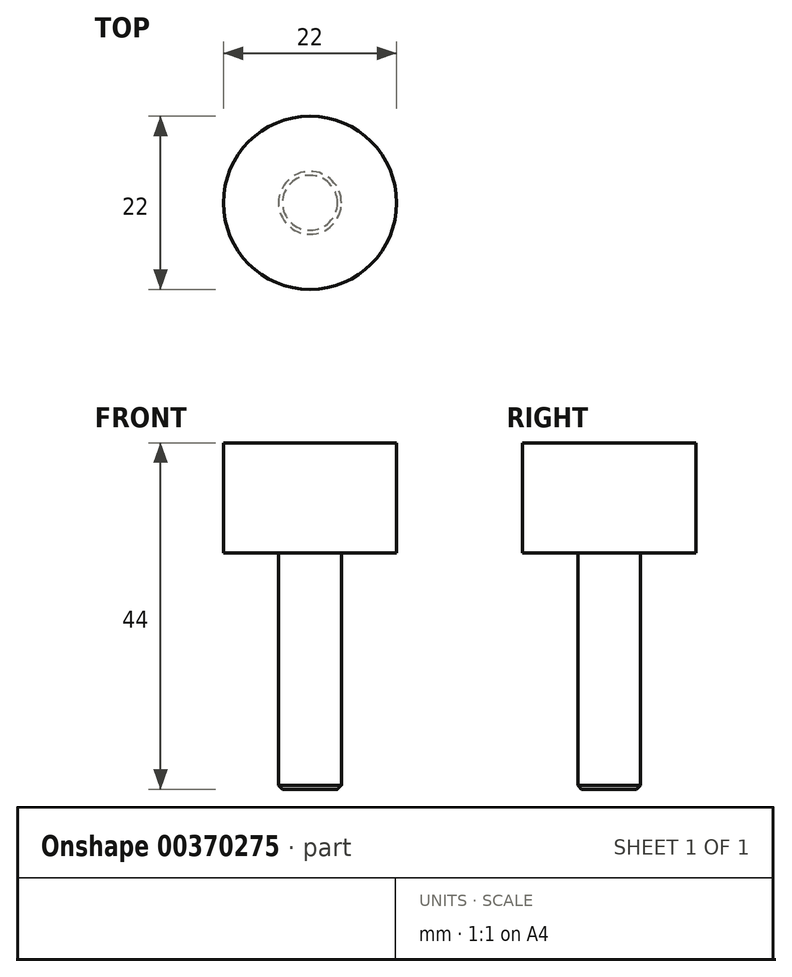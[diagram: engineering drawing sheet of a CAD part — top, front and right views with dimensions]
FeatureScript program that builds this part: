
annotation { "Feature Type Name" : "Feature", "Feature Type Description" : "" }
export const myFeature = defineFeature(function(context is Context, id is Id, definition is map)
    precondition{}
    {
        {
            var Q0;
            Q0=qCreatedBy(makeId("Top.planeOp"),FACE);
            var sketch = newSketch(context, id + "F0", { "sketchPlane" : qUnion([Q0])});
            skCircle(sketch, "E0", {"center": v(0, 0) * mm, "radius": 11 * mm});
            skSolve(sketch);
        }
        {
            var Q0;
            Q0=makeQuery(id+"F0.imprint","IMPRINT",FACE,{"disambiguationData":[TD([[makeQuery(id+"F0.imprint","IMPRINT",EDGE,{"derivedFrom":sQuery(id+"F0.wireOp",EDGE,"E0")}),1.0]])]});
            extrude(context, id + "F1", {"entities" : qUnion([Q0]), "depth" : 14 * mm});
        }
        {
            var Q0;
            Q0=qCreatedBy(makeId("Top.planeOp"),FACE);
            var sketch = newSketch(context, id + "F2", { "sketchPlane" : qUnion([Q0])});
            skCircle(sketch, "E1", {"center": v(0, 0) * mm, "radius": 4 * mm});
            skSolve(sketch);
        }
        {
            var Q0;
            Q0 = qSketchRegion(id + "F2", true);
            extrude(context, id + "F3", {"entities" : qUnion([Q0]), "operationType" : NewBodyOperationType.ADD, "oppositeDirection" : true, "depth" : 30 * mm});
        }
        {
            var Q0;
            Q0=makeQuery(id+"F3.opExtrude","CAP_EDGE",EDGE,{"disambiguationData":[OSD([sQuery(id+"F2.wireOp",EDGE,"E1")])],"isStart":false});
            chamfer(context, id + "F4", {"entities" : qUnion([Q0]), "width" : 0.5 * mm, "tangentPropagation" : true});
        }
    });
